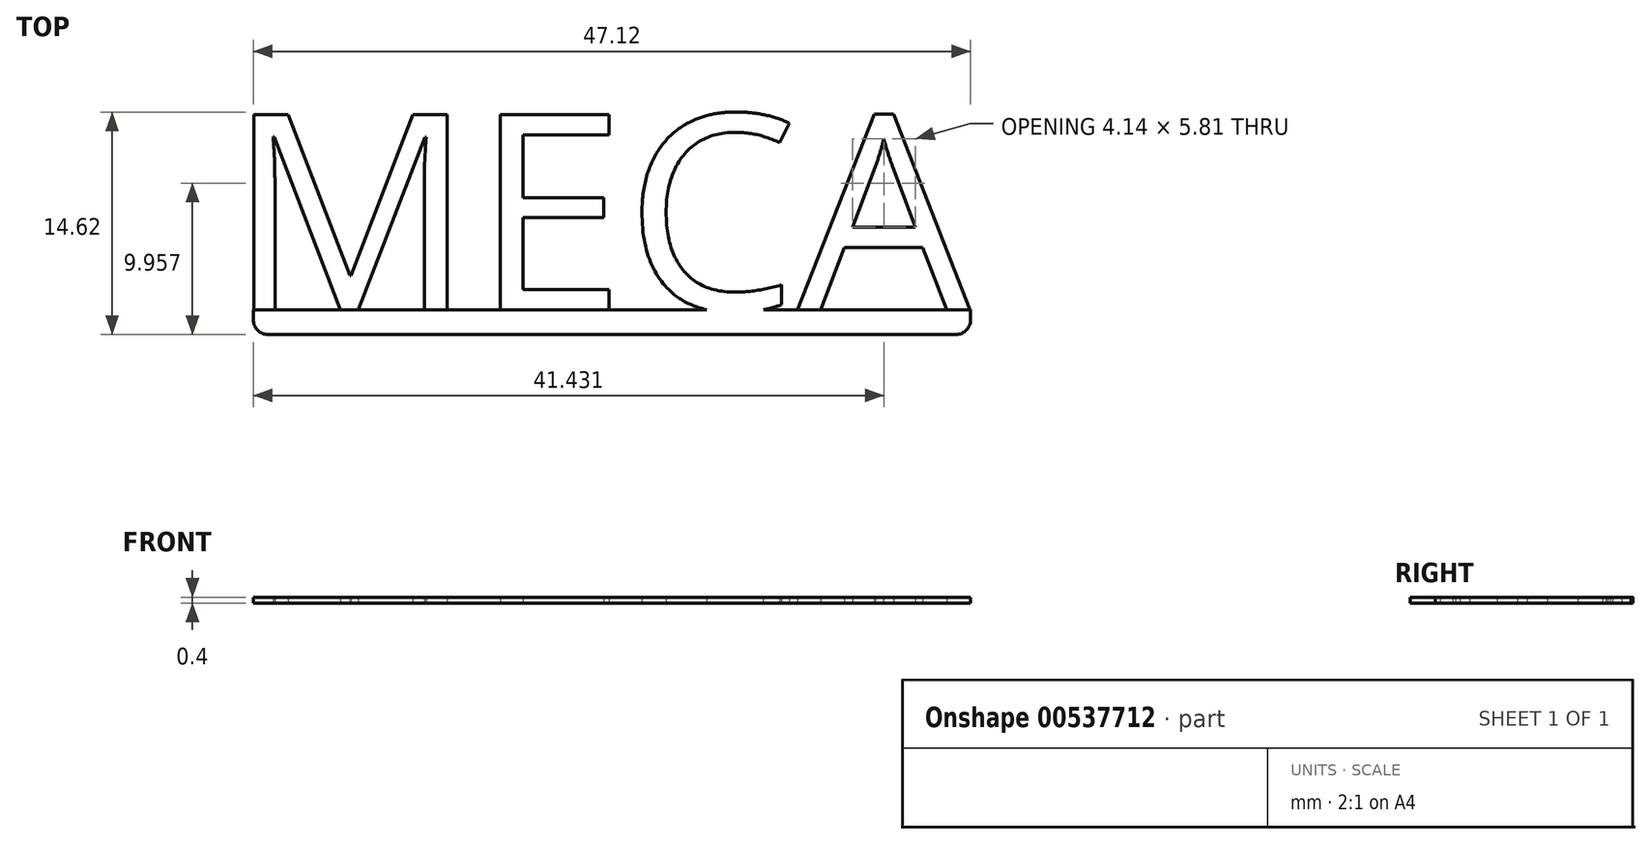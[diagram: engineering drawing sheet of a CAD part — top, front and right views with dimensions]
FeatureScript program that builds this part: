
annotation { "Feature Type Name" : "Feature", "Feature Type Description" : "" }
export const myFeature = defineFeature(function(context is Context, id is Id, definition is map)
    precondition{}
    {
        {
            var Q0;
            Q0=qCreatedBy(makeId("Top.planeOp"),FACE);
            var sketch = newSketch(context, id + "F0", { "sketchPlane" : qUnion([Q0])});
            skText(sketch, "E0", { "text": "MECA", "fontName": "OpenSans-Regular.ttf"});
            skLineSegment(sketch, "E1", {"start": v(-18.98, 6.45) * mm, "end": v(5.02, 6.45) * mm});
            skLineSegment(sketch, "E2", {"start": v(-12.63, -6.46) * mm, "end": v(-10.86, -6.46) * mm});
            skLineSegment(sketch, "E3", {"start": v(-10.86, -6.46) * mm, "end": v(-0.1, -6.46) * mm});
            skLineSegment(sketch, "E4", {"start": v(-0.16, -6.6) * mm, "end": v(-0.1, -6.46) * mm});
            skLineSegment(sketch, "E5", {"start": v(-0.16, -6.6) * mm, "end": v(-12.63, -6.6) * mm});
            skLineSegment(sketch, "E6.bottom", {"start": v(-30.6, -6.46) * mm, "end": v(16.51, -6.46) * mm});
            skLineSegment(sketch, "E6.top", {"start": v(-30.6, -8.1) * mm, "end": v(16.51, -8.1) * mm});
            skLineSegment(sketch, "E6.left", {"start": v(-30.6, -8.1) * mm, "end": v(-30.6, -6.46) * mm});
            skLineSegment(sketch, "E6.right", {"start": v(16.51, -8.1) * mm, "end": v(16.51, -6.46) * mm});
            const initialGuessF0  = {"E0": [-0.03233, -0.00646, 1, 0, 0.01291]};
            skSetInitialGuess(sketch, initialGuessF0);
            skSolve(sketch);
        }
        {
            var Q0;
            Q0=makeQuery(id+"F0.imprint","IMPRINT",FACE,{"disambiguationData":[TD([[makeQuery(id+"F0.imprint","IMPRINT",EDGE,{"derivedFrom":sQuery(id+"F0.wireOp",EDGE,"E0.sketch_text.stroke-30")}),-1.0]])]});
            var Q1;
            {var subQ1=sQuery(id+"F0.wireOp",EDGE,"E0.sketch_text.stroke-20");Q1=makeQuery(id+"F0.imprint","IMPRINT",FACE,{"disambiguationData":[TD([[makeQuery(id+"F0.imprint","IMPRINT",EDGE,{"derivedFrom":subQ1}),-1.0]])]});}
            var Q2;
            Q2=makeQuery(id+"F0.imprint","IMPRINT",FACE,{"disambiguationData":[TD([[makeQuery(id+"F0.imprint","IMPRINT",EDGE,{"derivedFrom":sQuery(id+"F0.wireOp",EDGE,"E0.sketch_text.stroke-0")}),-1.0]])]});
            var Q3;
            Q3=makeQuery(id+"F0.imprint","IMPRINT",FACE,{"disambiguationData":[TD([[makeQuery(id+"F0.imprint","IMPRINT",EDGE,{"derivedFrom":sQuery(id+"F0.wireOp",EDGE,"E0.sketch_text.stroke-45")}),-1.0]])]});
            var Q4;
            Q4 = qSketchRegion(id + "F0", true);
            extrude(context, id + "F1", {"entities" : qUnion([Q0, Q1, Q2, Q3, Q4]), "depth" : .4 * mm, "offsetDistance" : 25.4 * mm});
        }
        {
            var Q0;
            Q0=makeQuery(id+"F1.opExtrude","SWEPT_EDGE",EDGE,{"disambiguationData":[OSD([sQuery(id+"F0.wireOp",EDGE,"E6.top"),sQuery(id+"F0.wireOp",EDGE,"E6.left")])]});
            var Q1;
            Q1=makeQuery(id+"F1.opExtrude","SWEPT_EDGE",EDGE,{"disambiguationData":[OSD([sQuery(id+"F0.wireOp",EDGE,"E6.top"),sQuery(id+"F0.wireOp",EDGE,"E6.right")])]});
            fillet(context, id + "F2", {"entities" : qUnion([Q0, Q1]), "radius" : 0.97 * mm, "tangentPropagation" : true, "allowEdgeOverflow" : false});
        }
    });
